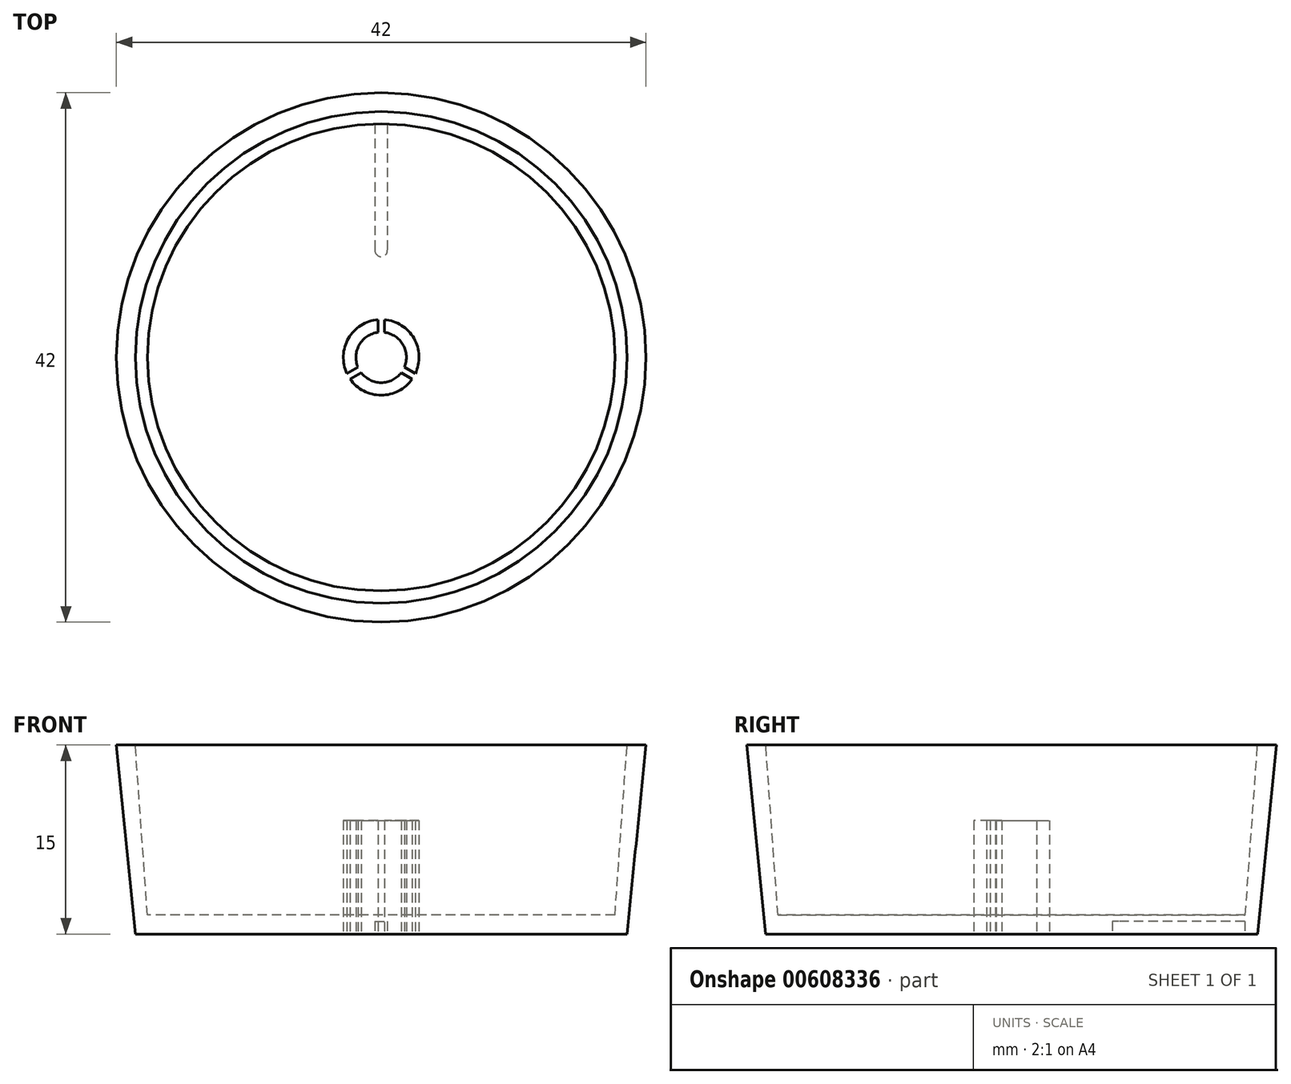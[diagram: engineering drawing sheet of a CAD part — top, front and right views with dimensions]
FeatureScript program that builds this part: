
annotation { "Feature Type Name" : "Feature", "Feature Type Description" : "" }
export const myFeature = defineFeature(function(context is Context, id is Id, definition is map)
    precondition{}
    {
        {
            var Q0;
            Q0=qCreatedBy(makeId("Top.planeOp"),FACE);
            var sketch = newSketch(context, id + "F0", { "sketchPlane" : qUnion([Q0])});
            skCircle(sketch, "E0", {"center": v(0, 0) * mm, "radius": 21 * mm});
            skCircle(sketch, "E1", {"center": v(0, 0) * mm, "radius": 18.5 * mm});
            skCircle(sketch, "E2", {"center": v(0, 0) * mm, "radius": 3 * mm});
            skCircle(sketch, "E3", {"center": v(0, 0) * mm, "radius": 2 * mm});
            skLineSegment(sketch, "E4", {"start": v(0.25, 1.98) * mm, "end": v(0.25, 2.99) * mm});
            skLineSegment(sketch, "E5", {"start": v(-0.25, 1.98) * mm, "end": v(-0.25, 2.99) * mm});
            skLineSegment(sketch, "E6", {"start": v(0.25, 1.98) * mm, "end": v(-0.25, 1.98) * mm, "construction": true});
            skPoint(sketch, "E7", {"position": v(0, 1.98) * mm});
            skLineSegment(sketch, "E8.1.0", {"start": v(-1.84, -0.78) * mm, "end": v(-2.71, -1.28) * mm});
            skLineSegment(sketch, "E8.1.1", {"start": v(-1.6, -1.2) * mm, "end": v(-2.46, -1.71) * mm});
            skLineSegment(sketch, "E8.2.0", {"start": v(1.6, -1.2) * mm, "end": v(2.46, -1.71) * mm});
            skLineSegment(sketch, "E8.2.1", {"start": v(1.84, -0.78) * mm, "end": v(2.71, -1.28) * mm});
            skLineSegment(sketch, "E9.bottom", {"start": v(-0.5, 18.5) * mm, "end": v(0.5, 18.5) * mm});
            skLineSegment(sketch, "E9.top", {"start": v(-0.5, 8.5) * mm, "end": v(0.5, 8.5) * mm});
            skLineSegment(sketch, "E9.left", {"start": v(-0.5, 18.5) * mm, "end": v(-0.5, 8.5) * mm});
            skLineSegment(sketch, "E9.right", {"start": v(0.5, 18.5) * mm, "end": v(0.5, 8.5) * mm});
            skCircle(sketch, "E10", {"center": v(0, 8.5) * mm, "radius": 0.5 * mm});
            skSolve(sketch);
        }
        {
            var Q0;
            Q0 = qSketchRegion(id + "F0", true);
            extrude(context, id + "F1", {"entities" : qUnion([Q0]), "depth" : 15 * mm, "offsetDistance" : 25 * mm});
        }
        {
            var Q0;
            Q0=makeQuery(id+"F0.imprint","IMPRINT",FACE,{"disambiguationData":[TD([[makeQuery(id+"F0.imprint","IMPRINT",EDGE,{"derivedFrom":sQuery(id+"F0.wireOp",EDGE,"E1")}),1.0]])]});
            var Q1;
            {var subQ0=sQuery(id+"F0.wireOp",EDGE,"E3");var subQ5=makeQuery(id+"F0.imprint","INTERSECT",VERTEX,{"derivedFrom":[subQ0,sQuery(id+"F0.wireOp",EDGE,"E4")]});Q1=makeQuery(id+"F0.imprint","IMPRINT",FACE,{"disambiguationData":[TD([[makeQuery(id+"F0.imprint","IMPRINT",EDGE,{"disambiguationData":[TD([[subQ5,-1.0]])],"derivedFrom":subQ0}),1.0]])]});}
            var Q2;
            {var subQ0=sQuery(id+"F0.wireOp",EDGE,"E5");Q2=makeQuery(id+"F0.imprint","IMPRINT",FACE,{"disambiguationData":[TD([[makeQuery(id+"F0.imprint","IMPRINT",EDGE,{"derivedFrom":subQ0}),1.0]])]});}
            var Q3;
            {var subQ0=sQuery(id+"F0.wireOp",EDGE,"E4");Q3=makeQuery(id+"F0.imprint","IMPRINT",FACE,{"disambiguationData":[TD([[makeQuery(id+"F0.imprint","IMPRINT",EDGE,{"derivedFrom":subQ0}),1.0]])]});}
            var Q4;
            {var subQ0=sQuery(id+"F0.wireOp",EDGE,"E8.1.1");Q4=makeQuery(id+"F0.imprint","IMPRINT",FACE,{"disambiguationData":[TD([[makeQuery(id+"F0.imprint","IMPRINT",EDGE,{"derivedFrom":subQ0}),1.0]])]});}
            var Q5;
            {var subQ0=sQuery(id+"F0.wireOp",EDGE,"E8.2.0");Q5=makeQuery(id+"F0.imprint","IMPRINT",FACE,{"disambiguationData":[TD([[makeQuery(id+"F0.imprint","IMPRINT",EDGE,{"derivedFrom":subQ0}),1.0]])]});}
            var Q6;
            {var subQ0=sQuery(id+"F0.wireOp",EDGE,"E4");Q6=makeQuery(id+"F0.imprint","IMPRINT",FACE,{"disambiguationData":[TD([[makeQuery(id+"F0.imprint","IMPRINT",EDGE,{"derivedFrom":subQ0}),-1.0]])]});}
            var Q7;
            {var subQ0=sQuery(id+"F0.wireOp",EDGE,"E8.1.0");Q7=makeQuery(id+"F0.imprint","IMPRINT",FACE,{"disambiguationData":[TD([[makeQuery(id+"F0.imprint","IMPRINT",EDGE,{"derivedFrom":subQ0}),1.0]])]});}
            var Q8;
            {var subQ8=sQuery(id+"F0.wireOp",EDGE,"E1");var subQ11=sQuery(id+"F0.wireOp",EDGE,"E9.left");var subQ12=makeQuery(id+"F0.imprint","INTERSECT",VERTEX,{"derivedFrom":[subQ8,subQ11]});Q8=makeQuery(id+"F0.imprint","IMPRINT",FACE,{"disambiguationData":[TD([[makeQuery(id+"F0.imprint","IMPRINT",EDGE,{"disambiguationData":[TD([[subQ12,-1.0]])],"derivedFrom":subQ8}),1.0]])]});}
            var Q9;
            {var subQ0=sQuery(id+"F0.wireOp",EDGE,"E9.top");Q9=makeQuery(id+"F0.imprint","IMPRINT",FACE,{"disambiguationData":[TD([[makeQuery(id+"F0.imprint","IMPRINT",EDGE,{"derivedFrom":subQ0}),-1.0]])]});}
            var Q10;
            {var subQ0=sQuery(id+"F0.wireOp",EDGE,"E9.top");Q10=makeQuery(id+"F0.imprint","IMPRINT",FACE,{"disambiguationData":[TD([[makeQuery(id+"F0.imprint","IMPRINT",EDGE,{"derivedFrom":subQ0}),1.0]])]});}
            var Q11;
            Q11=makeQuery(id+"F0.imprint","IMPRINT",FACE,{"disambiguationData":[TD([[makeQuery(id+"F0.imprint","IMPRINT",EDGE,{"derivedFrom":sQuery(id+"F0.wireOp",EDGE,"E9.bottom")}),-1.0]])]});
            extrude(context, id + "F2", {"entities" : qUnion([Q0, Q1, Q2, Q3, Q4, Q5, Q6, Q7, Q8, Q9, Q10, Q11]), "operationType" : NewBodyOperationType.ADD, "depth" : 1.5 * mm, "offsetDistance" : 25 * mm});
        }
        {
            var Q0;
            {var subQ0=sQuery(id+"F0.wireOp",EDGE,"E9.top");Q0=makeQuery(id+"F0.imprint","IMPRINT",FACE,{"disambiguationData":[TD([[makeQuery(id+"F0.imprint","IMPRINT",EDGE,{"derivedFrom":subQ0}),-1.0]])]});}
            var Q1;
            {var subQ0=sQuery(id+"F0.wireOp",EDGE,"E9.top");Q1=makeQuery(id+"F0.imprint","IMPRINT",FACE,{"disambiguationData":[TD([[makeQuery(id+"F0.imprint","IMPRINT",EDGE,{"derivedFrom":subQ0}),1.0]])]});}
            var Q2;
            {var subQ0=sQuery(id+"F0.wireOp",EDGE,"E9.left");var subQ1=sQuery(id+"F0.wireOp",EDGE,"E1");var subQ2=makeQuery(id+"F0.imprint","INTERSECT",VERTEX,{"derivedFrom":[subQ1,subQ0]});Q2=makeQuery(id+"F0.imprint","IMPRINT",FACE,{"disambiguationData":[TD([[makeQuery(id+"F0.imprint","IMPRINT",EDGE,{"disambiguationData":[TD([[subQ2,1.0]])],"derivedFrom":subQ1}),1.0]])]});}
            var Q3;
            {var subQ5=sQuery(id+"F0.wireOp",EDGE,"E9.bottom");Q3=makeQuery(id+"F0.imprint","IMPRINT",FACE,{"disambiguationData":[TD([[makeQuery(id+"F0.imprint","IMPRINT",EDGE,{"derivedFrom":subQ5}),-1.0]])]});}
            extrude(context, id + "F3", {"entities" : qUnion([Q0, Q1, Q2, Q3]), "operationType" : NewBodyOperationType.REMOVE, "oppositeDirection" : true, "depth" : -1 * mm, "offsetDistance" : 25 * mm});
        }
        {
            var Q0;
            {var subQ0=sQuery(id+"F0.wireOp",EDGE,"E5");Q0=makeQuery(id+"F0.imprint","IMPRINT",FACE,{"disambiguationData":[TD([[makeQuery(id+"F0.imprint","IMPRINT",EDGE,{"derivedFrom":subQ0}),1.0]])]});}
            var Q1;
            {var subQ0=sQuery(id+"F0.wireOp",EDGE,"E4");Q1=makeQuery(id+"F0.imprint","IMPRINT",FACE,{"disambiguationData":[TD([[makeQuery(id+"F0.imprint","IMPRINT",EDGE,{"derivedFrom":subQ0}),-1.0]])]});}
            var Q2;
            {var subQ0=sQuery(id+"F0.wireOp",EDGE,"E8.1.1");Q2=makeQuery(id+"F0.imprint","IMPRINT",FACE,{"disambiguationData":[TD([[makeQuery(id+"F0.imprint","IMPRINT",EDGE,{"derivedFrom":subQ0}),1.0]])]});}
            extrude(context, id + "F4", {"entities" : qUnion([Q0, Q1, Q2]), "depth" : 9 * mm, "offsetDistance" : 25 * mm});
        }
        {
            var Q0;
            Q0=makeQuery(id+"F1.opExtrude","CAP_EDGE",EDGE,{"disambiguationData":[OSD([sQuery(id+"F0.wireOp",EDGE,"E0")])],"isStart":true});
            chamfer(context, id + "F5", {"entities" : qUnion([Q0]), "chamferType" : ChamferType.TWO_OFFSETS, "width1" : 15 * mm, "oppositeDirection" : false, "width2" : 1.5 * mm, "tangentPropagation" : true});
        }
        {
            var Q0;
            Q0=makeQuery(id+"F1.opExtrude","CAP_EDGE",EDGE,{"disambiguationData":[OSD([sQuery(id+"F0.wireOp",EDGE,"E1")])],"isStart":false});
            chamfer(context, id + "F6", {"entities" : qUnion([Q0]), "chamferType" : ChamferType.TWO_OFFSETS, "width1" : 14 * mm, "oppositeDirection" : false, "width2" : 1 * mm, "tangentPropagation" : true});
        }
    });
